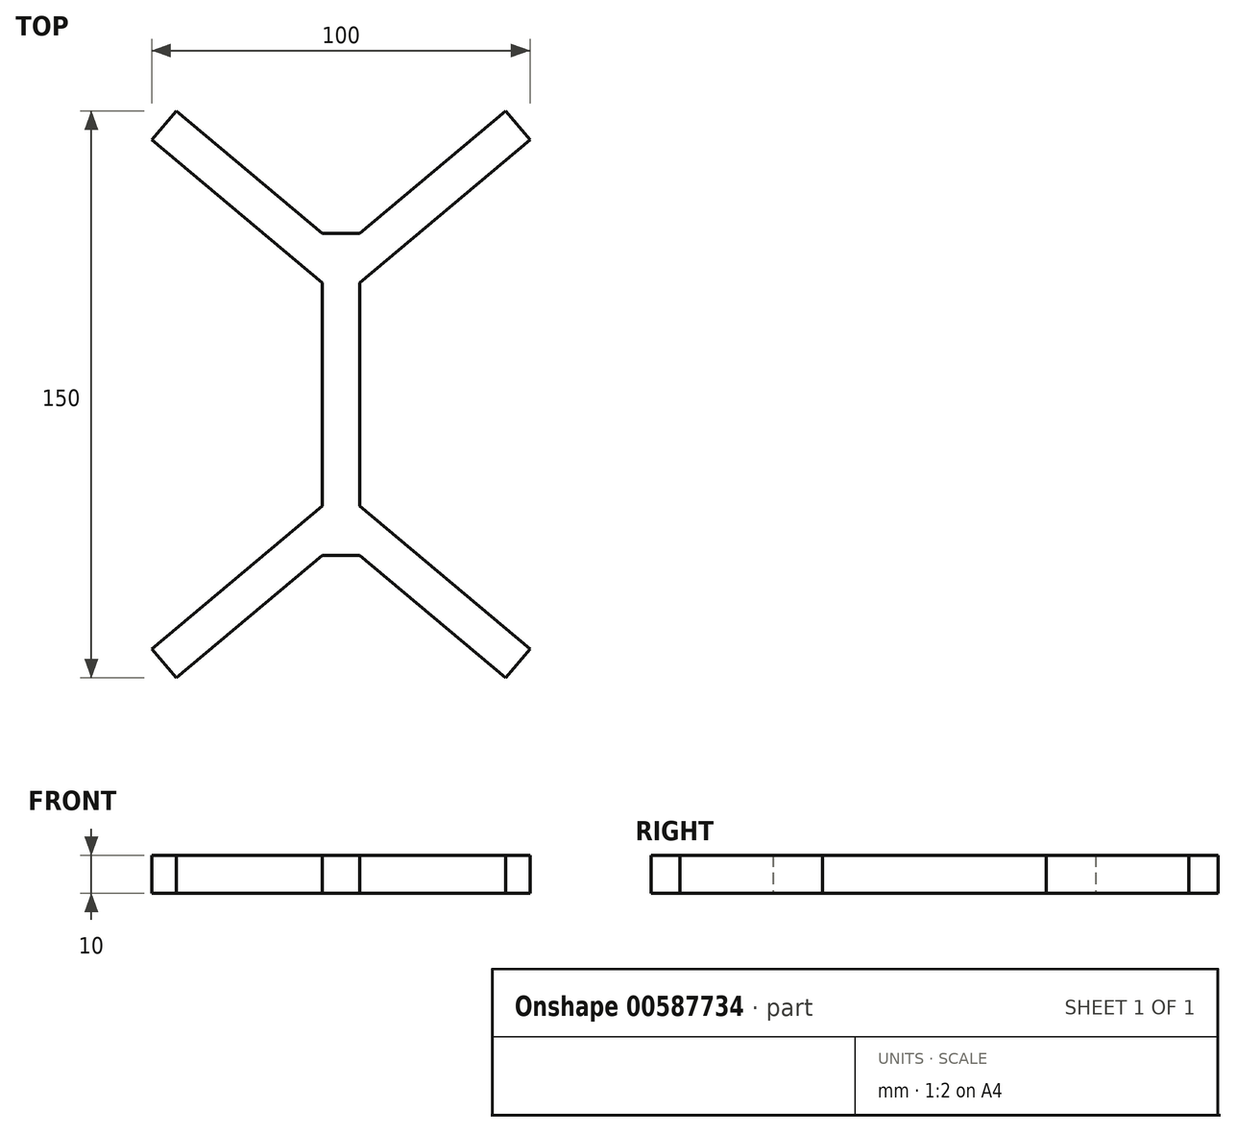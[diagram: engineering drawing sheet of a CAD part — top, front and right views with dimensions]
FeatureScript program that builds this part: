
annotation { "Feature Type Name" : "Feature", "Feature Type Description" : "" }
export const myFeature = defineFeature(function(context is Context, id is Id, definition is map)
    precondition{}
    {
        {
            var Q0;
            Q0=qCreatedBy(makeId("Top.planeOp"),FACE);
            var sketch = newSketch(context, id + "F0", { "sketchPlane" : qUnion([Q0])});
            skLineSegment(sketch, "E0.bottom", {"start": v(-5, 42.63) * mm, "end": v(5, 42.63) * mm});
            skLineSegment(sketch, "E0.top", {"start": v(-5, -42.63) * mm, "end": v(5, -42.63) * mm});
            skLineSegment(sketch, "E0.left", {"start": v(-5, 29.58) * mm, "end": v(-5, -29.58) * mm});
            skLineSegment(sketch, "E0.right", {"start": v(5, 29.58) * mm, "end": v(5, -29.58) * mm});
            skPoint(sketch, "E0.middle", {"position": v(0, 0) * mm});
            skLineSegment(sketch, "E1", {"start": v(-5, 42.63) * mm, "end": v(-43.57, 75) * mm});
            skLineSegment(sketch, "E2", {"start": v(-43.57, 75) * mm, "end": v(-50, 67.34) * mm});
            skLineSegment(sketch, "E3", {"start": v(-50, 67.34) * mm, "end": v(-5, 29.58) * mm});
            skLineSegment(sketch, "E4", {"start": v(5, 42.63) * mm, "end": v(43.57, 75) * mm});
            skLineSegment(sketch, "E5", {"start": v(43.57, 75) * mm, "end": v(50, 67.34) * mm});
            skLineSegment(sketch, "E6", {"start": v(50, 67.34) * mm, "end": v(5, 29.58) * mm});
            skLineSegment(sketch, "E7", {"start": v(-5, -42.63) * mm, "end": v(-43.57, -75) * mm});
            skLineSegment(sketch, "E8", {"start": v(-43.57, -75) * mm, "end": v(-50, -67.34) * mm});
            skLineSegment(sketch, "E9", {"start": v(-50, -67.34) * mm, "end": v(-5, -29.58) * mm});
            skLineSegment(sketch, "E10", {"start": v(5, -42.63) * mm, "end": v(43.57, -75) * mm});
            skLineSegment(sketch, "E11", {"start": v(43.57, -75) * mm, "end": v(50, -67.34) * mm});
            skLineSegment(sketch, "E12", {"start": v(50, -67.34) * mm, "end": v(5, -29.58) * mm});
            skSolve(sketch);
        }
        {
            var Q0;
            Q0=makeQuery(id+"F0.imprint","IMPRINT",FACE,{"disambiguationData":[TD([[makeQuery(id+"F0.imprint","IMPRINT",EDGE,{"derivedFrom":sQuery(id+"F0.wireOp",EDGE,"E0.bottom")}),-1.0]])]});
            extrude(context, id + "F1", {"entities" : qUnion([Q0]), "endBound" : BoundingType.SYMMETRIC, "depth" : 10 * mm, "offsetDistance" : 25 * mm});
        }
    });
